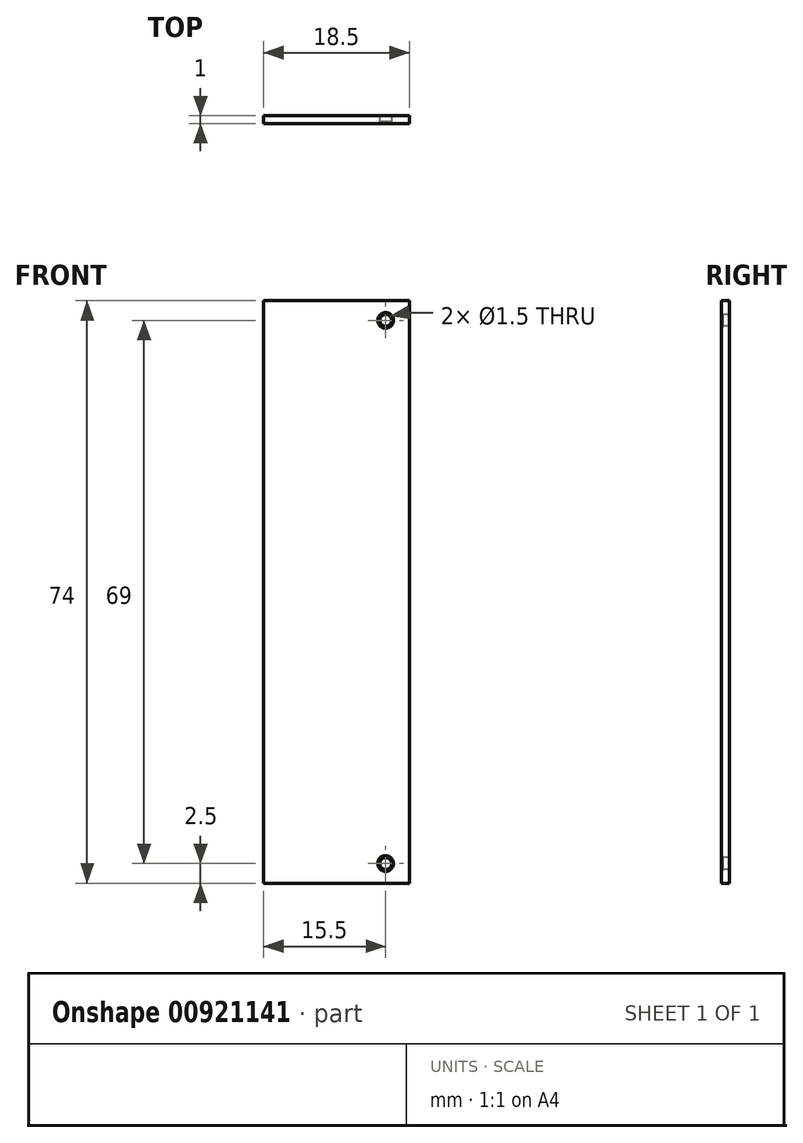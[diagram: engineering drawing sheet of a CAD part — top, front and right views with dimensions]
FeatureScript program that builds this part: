
annotation { "Feature Type Name" : "Feature", "Feature Type Description" : "" }
export const myFeature = defineFeature(function(context is Context, id is Id, definition is map)
    precondition{}
    {
        {
            var Q0;
            Q0=qCreatedBy(makeId("Front.planeOp"),FACE);
            var sketch = newSketch(context, id + "F0", { "sketchPlane" : qUnion([Q0])});
            skLineSegment(sketch, "E0.bottom", {"start": v(9.25, -37) * mm, "end": v(-9.25, -37) * mm});
            skLineSegment(sketch, "E0.top", {"start": v(9.25, 37) * mm, "end": v(-9.25, 37) * mm});
            skLineSegment(sketch, "E0.left", {"start": v(9.25, -37) * mm, "end": v(9.25, 37) * mm});
            skLineSegment(sketch, "E0.right", {"start": v(-9.25, -37) * mm, "end": v(-9.25, 37) * mm});
            skPoint(sketch, "E0.middle", {"position": v(0, 0) * mm});
            skCircle(sketch, "E1", {"center": v(6.25, 34.5) * mm, "radius": 1 * mm});
            skCircle(sketch, "E2", {"center": v(6.25, -34.5) * mm, "radius": 1 * mm});
            skLineSegment(sketch, "E3", {"start": v(-18.87, 0) * mm, "end": v(17.68, 0) * mm, "construction": true});
            skCircle(sketch, "E4", {"center": v(6.25, 34.5) * mm, "radius": 0.75 * mm});
            skCircle(sketch, "E5", {"center": v(6.25, -34.5) * mm, "radius": 0.75 * mm});
            skSolve(sketch);
        }
        {
            var Q0;
            Q0=makeQuery(id+"F0.imprint","IMPRINT",FACE,{"disambiguationData":[TD([[makeQuery(id+"F0.imprint","IMPRINT",EDGE,{"derivedFrom":sQuery(id+"F0.wireOp",EDGE,"E0.bottom")}),-1.0]])]});
            var Q1;
            Q1=makeQuery(id+"F0.imprint","IMPRINT",FACE,{"disambiguationData":[TD([[makeQuery(id+"F0.imprint","IMPRINT",EDGE,{"derivedFrom":sQuery(id+"F0.wireOp",EDGE,"E2")}),1.0]])]});
            var Q2;
            Q2=makeQuery(id+"F0.imprint","IMPRINT",FACE,{"disambiguationData":[TD([[makeQuery(id+"F0.imprint","IMPRINT",EDGE,{"derivedFrom":sQuery(id+"F0.wireOp",EDGE,"E1")}),1.0]])]});
            extrude(context, id + "F1", {"entities" : qUnion([Q0, Q1, Q2]), "oppositeDirection" : true, "depth" : 1 * mm, "offsetDistance" : 25 * mm});
        }
        {
            var Q0;
            Q0=makeQuery(id+"F1.opExtrude","CAP_EDGE",EDGE,{"disambiguationData":[OSD([sQuery(id+"F0.wireOp",EDGE,"E5")])],"isStart":true});
            var Q1;
            Q1=makeQuery(id+"F1.opExtrude","CAP_EDGE",EDGE,{"disambiguationData":[OSD([sQuery(id+"F0.wireOp",EDGE,"E4")])],"isStart":true});
            chamfer(context, id + "F2", {"entities" : qUnion([Q0, Q1]), "width" : 0.25 * mm, "tangentPropagation" : true});
        }
    });
